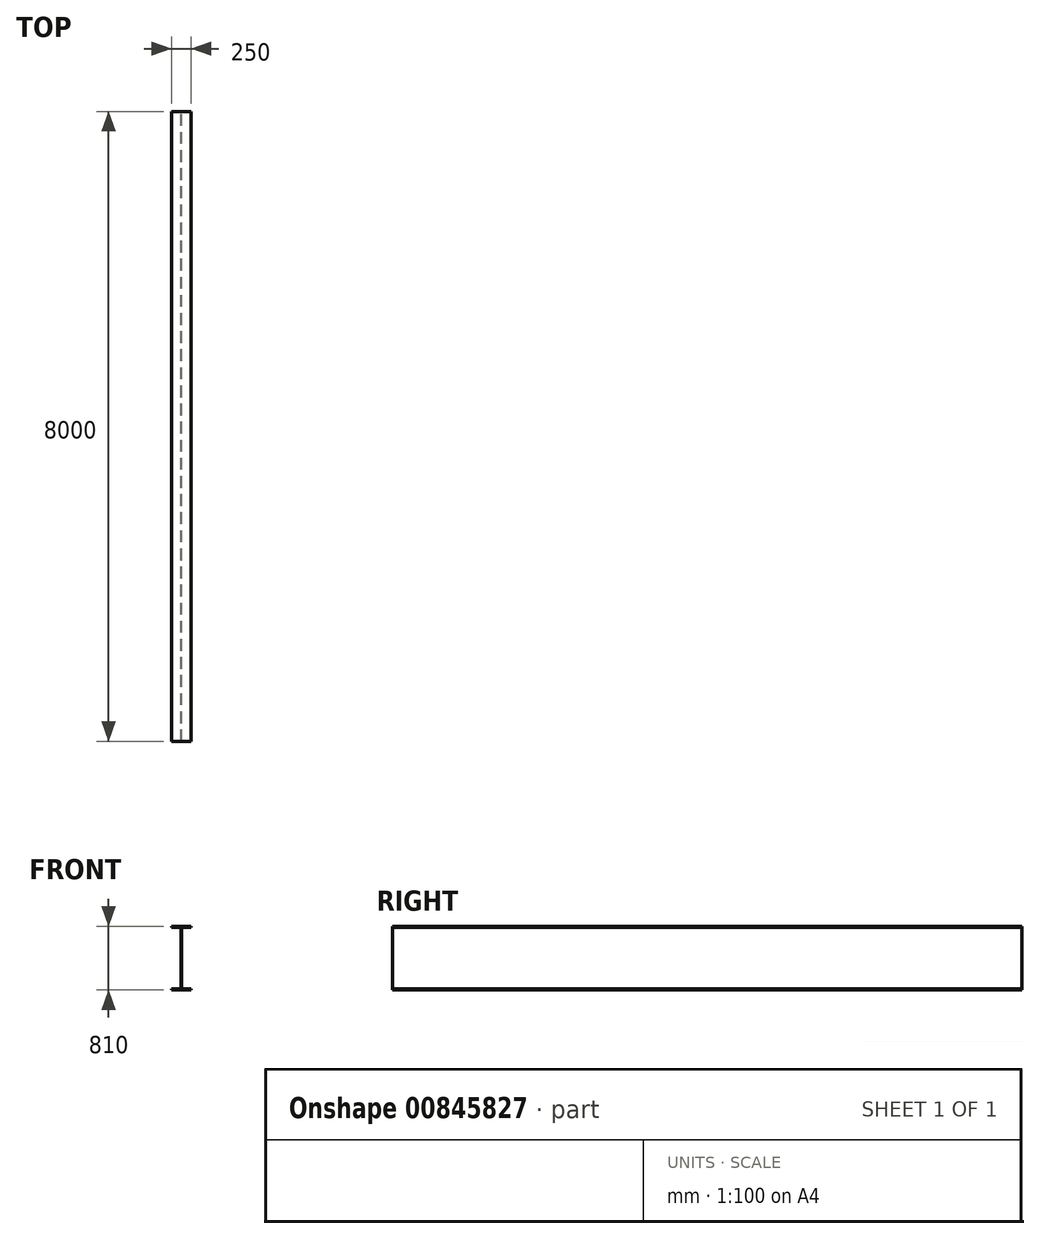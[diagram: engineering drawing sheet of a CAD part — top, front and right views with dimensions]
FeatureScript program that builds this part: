
annotation { "Feature Type Name" : "Feature", "Feature Type Description" : "" }
export const myFeature = defineFeature(function(context is Context, id is Id, definition is map)
    precondition{}
    {
        {
            var Q0;
            Q0=qCreatedBy(makeId("Front.planeOp"),FACE);
            var sketch = newSketch(context, id + "F0", { "sketchPlane" : qUnion([Q0])});
            skLineSegment(sketch, "E0.bottom", {"start": v(-131.13, 736.66) * mm, "end": v(118.87, 736.66) * mm});
            skLineSegment(sketch, "E0.top", {"start": v(-131.13, -73.34) * mm, "end": v(118.87, -73.34) * mm});
            skLineSegment(sketch, "E0.left", {"start": v(-131.13, 736.66) * mm, "end": v(-131.13, 721.66) * mm});
            skLineSegment(sketch, "E0.right", {"start": v(118.87, 736.66) * mm, "end": v(118.87, 721.66) * mm});
            skLineSegment(sketch, "E1.left", {"start": v(-131.13, 736.66) * mm, "end": v(-131.13, 736.66) * mm});
            skLineSegment(sketch, "E1.right", {"start": v(118.87, 736.66) * mm, "end": v(118.87, 736.66) * mm});
            skLineSegment(sketch, "E2.bottom", {"start": v(118.87, 721.66) * mm, "end": v(-1.13, 721.66) * mm});
            skLineSegment(sketch, "E2.top", {"start": v(118.87, -58.34) * mm, "end": v(-1.13, -58.34) * mm});
            skLineSegment(sketch, "E2.right", {"start": v(-1.13, 721.66) * mm, "end": v(-1.13, -58.34) * mm});
            skLineSegment(sketch, "E3.bottom", {"start": v(-1.13, 721.66) * mm, "end": v(118.87, 721.66) * mm});
            skLineSegment(sketch, "E3.top", {"start": v(-1.13, 721.66) * mm, "end": v(118.87, 721.66) * mm});
            skLineSegment(sketch, "E3.left", {"start": v(-1.13, 721.66) * mm, "end": v(-1.13, 721.66) * mm});
            skLineSegment(sketch, "E3.right", {"start": v(118.87, 721.66) * mm, "end": v(118.87, 721.66) * mm});
            skLineSegment(sketch, "E4.bottom", {"start": v(-131.13, 721.66) * mm, "end": v(-11.13, 721.66) * mm});
            skLineSegment(sketch, "E4.top", {"start": v(-131.13, -58.34) * mm, "end": v(-11.13, -58.34) * mm});
            skLineSegment(sketch, "E4.right", {"start": v(-11.13, 721.66) * mm, "end": v(-11.13, -58.34) * mm});
            skLineSegment(sketch, "E5.trimOffspring", {"start": v(-131.13, -58.34) * mm, "end": v(-131.13, -73.34) * mm});
            skLineSegment(sketch, "E6.trimOffspring", {"start": v(118.87, -58.34) * mm, "end": v(118.87, -73.34) * mm});
            skSolve(sketch);
        }
        {
            var Q0;
            Q0 = qSketchRegion(id + "F0", true);
            extrude(context, id + "F1", {"entities" : qUnion([Q0]), "depth" : 8000 * mm, "offsetDistance" : 25 * mm});
        }
    });
